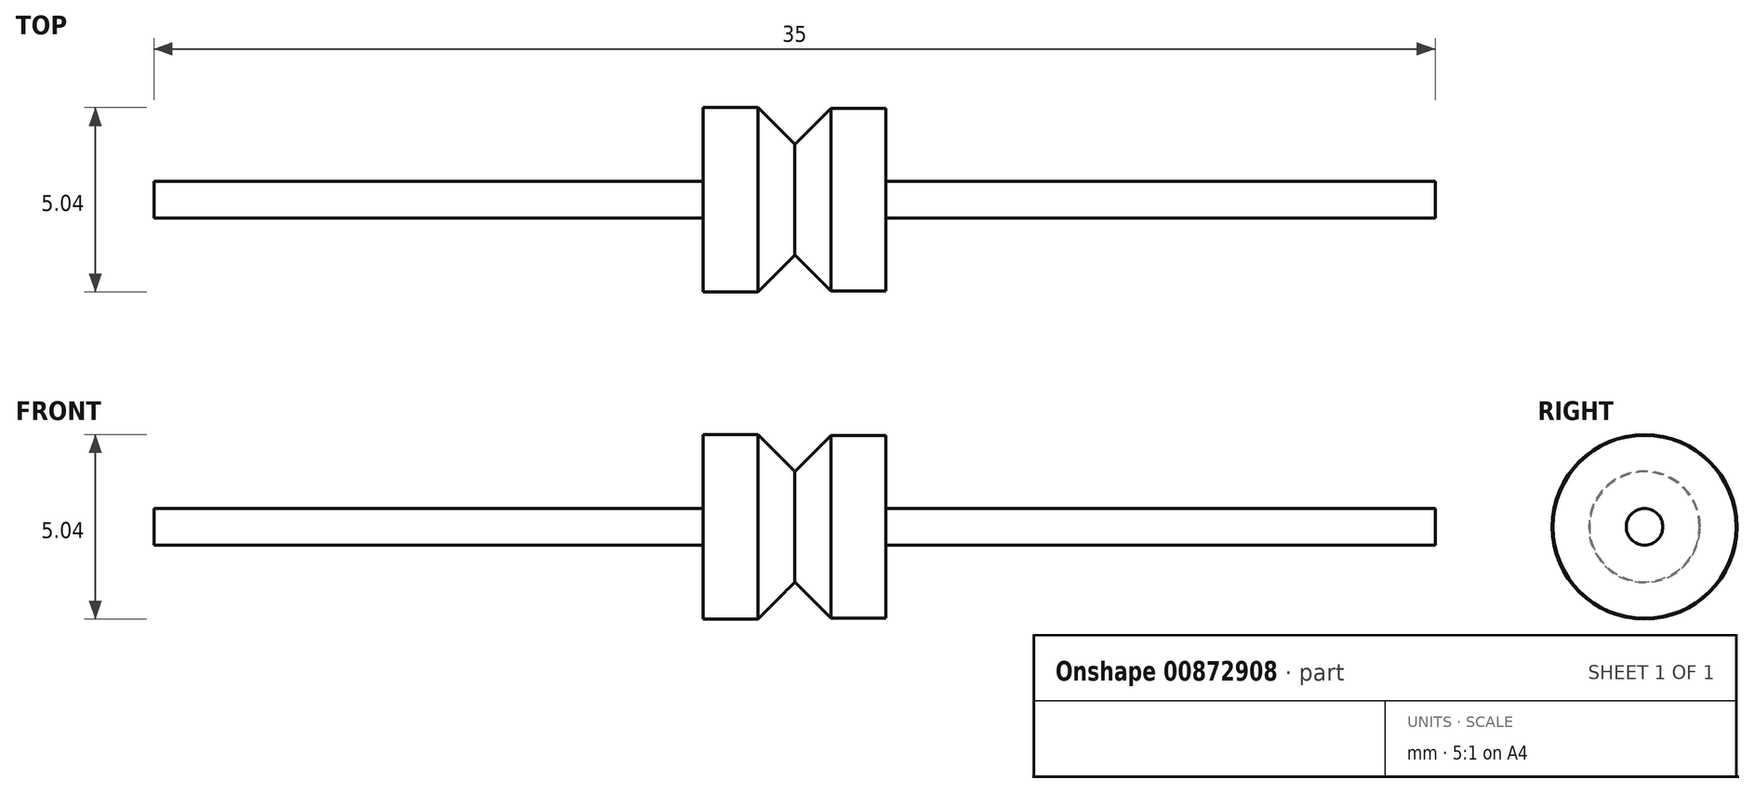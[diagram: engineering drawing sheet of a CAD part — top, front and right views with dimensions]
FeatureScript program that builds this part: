
annotation { "Feature Type Name" : "Feature", "Feature Type Description" : "" }
export const myFeature = defineFeature(function(context is Context, id is Id, definition is map)
    precondition{}
    {
        {
            var Q0;
            Q0=qCreatedBy(makeId("Right.planeOp"),FACE);
            var sketch = newSketch(context, id + "F0", { "sketchPlane" : qUnion([Q0])});
            skCircle(sketch, "E0", {"center": v(0, 0) * mm, "radius": 0.5 * mm});
            skSolve(sketch);
        }
        {
            var Q0;
            Q0 = qSketchRegion(id + "F0", true);
            extrude(context, id + "F1", {"entities" : qUnion([Q0]), "endBound" : BoundingType.SYMMETRIC, "depth" : 35 * mm, "offsetDistance" : 25 * mm});
        }
        {
            var Q0;
            Q0=qCreatedBy(makeId("Right.planeOp"),FACE);
            var sketch = newSketch(context, id + "F2", { "sketchPlane" : qUnion([Q0])});
            skCircle(sketch, "E1", {"center": v(0, 0) * mm, "radius": 2.5 * mm});
            skSolve(sketch);
        }
        {
            var Q0;
            Q0 = qSketchRegion(id + "F2", true);
            extrude(context, id + "F3", {"entities" : qUnion([Q0]), "operationType" : NewBodyOperationType.ADD, "depth" : 2.5 * mm, "offsetDistance" : 25 * mm});
        }
        {
            var Q0;
            Q0=makeQuery(id+"F3.opExtrude","CAP_EDGE",EDGE,{"disambiguationData":[OSD([sQuery(id+"F2.wireOp",EDGE,"E1")])],"isStart":true});
            chamfer(context, id + "F4", {"entities" : qUnion([Q0]), "width" : 1 * mm, "tangentPropagation" : true});
        }
        {
            var Q0;
            Q0=qCreatedBy(makeId("Right.planeOp"),FACE);
            var sketch = newSketch(context, id + "F5", { "sketchPlane" : qUnion([Q0])});
            skCircle(sketch, "E2", {"center": v(0, 0) * mm, "radius": 2.52 * mm});
            skSolve(sketch);
        }
        {
            var Q0;
            Q0 = qSketchRegion(id + "F5", true);
            extrude(context, id + "F6", {"entities" : qUnion([Q0]), "operationType" : NewBodyOperationType.ADD, "oppositeDirection" : true, "depth" : 2.5 * mm, "offsetDistance" : 25 * mm});
        }
        {
            var Q0;
            Q0=makeQuery(id+"F6.opExtrude","CAP_EDGE",EDGE,{"disambiguationData":[OSD([sQuery(id+"F5.wireOp",EDGE,"E2")])],"isStart":true});
            chamfer(context, id + "F7", {"entities" : qUnion([Q0]), "width" : 1 * mm, "tangentPropagation" : true});
        }
    });
